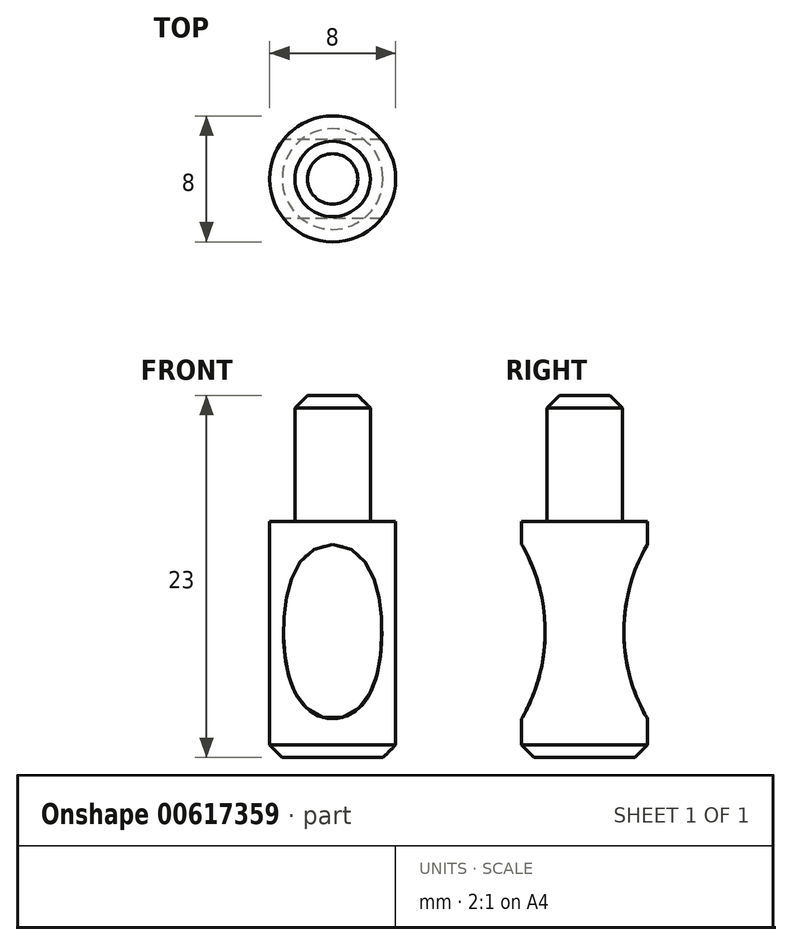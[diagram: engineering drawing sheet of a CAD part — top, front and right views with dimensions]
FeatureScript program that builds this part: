
annotation { "Feature Type Name" : "Feature", "Feature Type Description" : "" }
export const myFeature = defineFeature(function(context is Context, id is Id, definition is map)
    precondition{}
    {
        {
            var Q0;
            Q0=qCreatedBy(makeId("Top.planeOp"),FACE);
            var sketch = newSketch(context, id + "F0", { "sketchPlane" : qUnion([Q0])});
            skCircle(sketch, "E0", {"center": v(0, 0) * mm, "radius": 4 * mm});
            skSolve(sketch);
        }
        {
            var Q0;
            Q0=makeQuery(id+"F0.imprint","IMPRINT",FACE,{"disambiguationData":[TD([[makeQuery(id+"F0.imprint","IMPRINT",EDGE,{"derivedFrom":sQuery(id+"F0.wireOp",EDGE,"E0")}),1.0]])]});
            extrude(context, id + "F1", {"entities" : qUnion([Q0]), "depth" : 15 * mm, "offsetDistance" : 25 * mm});
        }
        {
            var Q0;
            Q0=makeQuery(id+"F1.opExtrude","CAP_FACE",FACE,{"disambiguationData":[OSD([sQuery(id+"F0.wireOp",EDGE,"E0")])],"isStart":false});
            var sketch = newSketch(context, id + "F2", { "sketchPlane" : qUnion([Q0])});
            skCircle(sketch, "E1", {"center": v(0, 0) * mm, "radius": 2.4 * mm});
            skSolve(sketch);
        }
        {
            var Q0;
            Q0 = qSketchRegion(id + "F2", true);
            extrude(context, id + "F3", {"entities" : qUnion([Q0]), "operationType" : NewBodyOperationType.ADD, "depth" : 8 * mm, "offsetDistance" : 25 * mm});
        }
        {
            var Q0;
            Q0=makeQuery(id+"F3.opExtrude","CAP_EDGE",EDGE,{"disambiguationData":[OSD([sQuery(id+"F2.wireOp",EDGE,"E1")])],"isStart":false});
            var Q1;
            Q1=makeQuery(id+"F1.opExtrude","CAP_EDGE",EDGE,{"disambiguationData":[OSD([sQuery(id+"F0.wireOp",EDGE,"E0")])],"isStart":true});
            chamfer(context, id + "F4", {"entities" : qUnion([Q0, Q1]), "width" : 0.8 * mm, "tangentPropagation" : true});
        }
        {
            var Q0;
            Q0=qCreatedBy(makeId("Right.planeOp"),FACE);
            var sketch = newSketch(context, id + "F5", { "sketchPlane" : qUnion([Q0])});
            skCircle(sketch, "E2", {"center": v(-13.5, 8) * mm, "radius": 11 * mm});
            skCircle(sketch, "E3", {"center": v(13.5, 8) * mm, "radius": 11 * mm});
            skSolve(sketch);
        }
        {
            var Q0;
            Q0 = qSketchRegion(id + "F5", true);
            extrude(context, id + "F6", {"entities" : qUnion([Q0]), "operationType" : NewBodyOperationType.REMOVE, "endBound" : BoundingType.SYMMETRIC, "depth" : 10 * mm, "offsetDistance" : 25 * mm});
        }
    });
